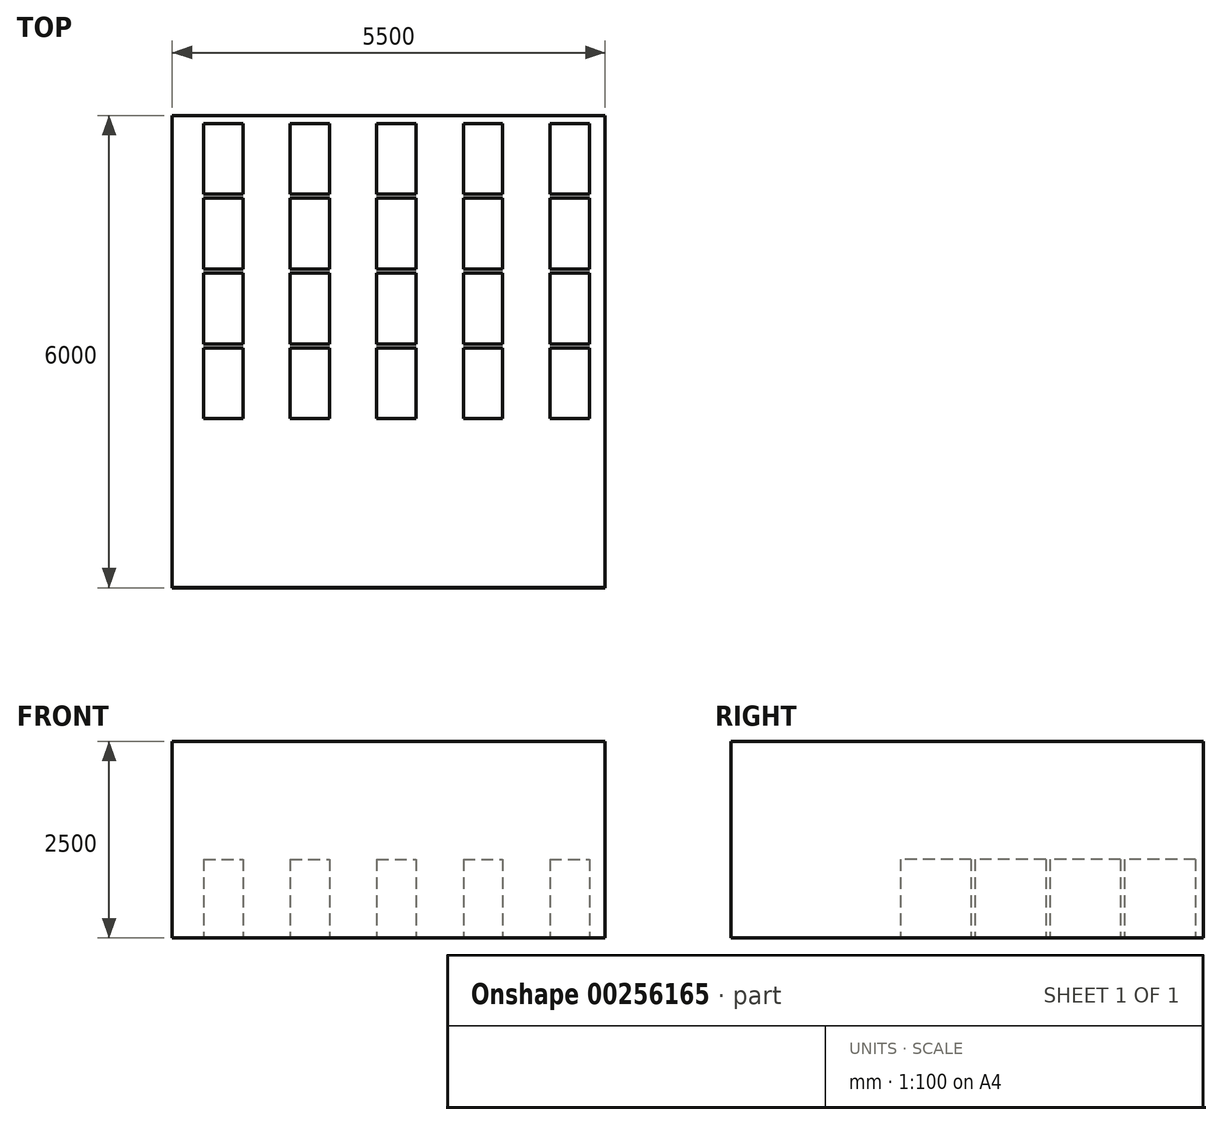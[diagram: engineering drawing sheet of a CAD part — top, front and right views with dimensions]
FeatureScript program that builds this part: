
annotation { "Feature Type Name" : "Feature", "Feature Type Description" : "" }
export const myFeature = defineFeature(function(context is Context, id is Id, definition is map)
    precondition{}
    {
        {
            var Q0;
            Q0=qCreatedBy(makeId("Top.planeOp"),FACE);
            var sketch = newSketch(context, id + "F0", { "sketchPlane" : qUnion([Q0])});
            skLineSegment(sketch, "E0.bottom", {"start": v(0, 0) * mm, "end": v(5500, 0) * mm});
            skLineSegment(sketch, "E0.top", {"start": v(0, 6000) * mm, "end": v(5500, 6000) * mm});
            skLineSegment(sketch, "E0.left", {"start": v(0, 0) * mm, "end": v(0, 6000) * mm});
            skLineSegment(sketch, "E0.right", {"start": v(5500, 0) * mm, "end": v(5500, 6000) * mm});
            skSolve(sketch);
        }
        {
            var Q0;
            Q0 = qSketchRegion(id + "F0", true);
            extrude(context, id + "F1", {"entities" : qUnion([Q0]), "depth" : 2500 * mm});
        }
        {
            var Q0;
            Q0=makeQuery(id+"F1.opExtrude","CAP_FACE",FACE,{"disambiguationData":[OSD([sQuery(id+"F0.wireOp",EDGE,"E0.bottom"),sQuery(id+"F0.wireOp",EDGE,"E0.top"),sQuery(id+"F0.wireOp",EDGE,"E0.left"),sQuery(id+"F0.wireOp",EDGE,"E0.right")])],"isStart":false});
            shell(context, id + "F2", {"entities" : qUnion([Q0]), "thickness" : 1.5 * mm});
        }
        {
            var Q0;
            Q0=makeQuery(id+"F2.opShell","OFFSET_FACE",FACE,{"disambiguationData":[OSD([sQuery(id+"F0.wireOp",EDGE,"E0.bottom"),sQuery(id+"F0.wireOp",EDGE,"E0.top"),sQuery(id+"F0.wireOp",EDGE,"E0.left"),sQuery(id+"F0.wireOp",EDGE,"E0.right")])]});
            var sketch = newSketch(context, id + "F3", { "sketchPlane" : qUnion([Q0])});
            skLineSegment(sketch, "E1.bottom", {"start": v(4798.5, 5898.5) * mm, "end": v(5298.5, 5898.5) * mm});
            skLineSegment(sketch, "E1.top", {"start": v(4798.5, 4998.5) * mm, "end": v(5298.5, 4998.5) * mm});
            skLineSegment(sketch, "E1.left", {"start": v(4798.5, 5898.5) * mm, "end": v(4798.5, 4998.5) * mm});
            skLineSegment(sketch, "E1.right", {"start": v(5298.5, 5898.5) * mm, "end": v(5298.5, 4998.5) * mm});
            skLineSegment(sketch, "E2.0.1.0", {"start": v(4798.5, 4948.5) * mm, "end": v(5298.5, 4948.5) * mm});
            skLineSegment(sketch, "E2.0.1.1", {"start": v(5298.5, 4948.5) * mm, "end": v(5298.5, 4048.5) * mm});
            skLineSegment(sketch, "E2.0.1.2", {"start": v(4798.5, 4048.5) * mm, "end": v(5298.5, 4048.5) * mm});
            skLineSegment(sketch, "E2.0.1.3", {"start": v(4798.5, 4948.5) * mm, "end": v(4798.5, 4048.5) * mm});
            skLineSegment(sketch, "E2.0.2.0", {"start": v(4798.5, 3998.5) * mm, "end": v(5298.5, 3998.5) * mm});
            skLineSegment(sketch, "E2.0.2.1", {"start": v(5298.5, 3998.5) * mm, "end": v(5298.5, 3098.5) * mm});
            skLineSegment(sketch, "E2.0.2.2", {"start": v(4798.5, 3098.5) * mm, "end": v(5298.5, 3098.5) * mm});
            skLineSegment(sketch, "E2.0.2.3", {"start": v(4798.5, 3998.5) * mm, "end": v(4798.5, 3098.5) * mm});
            skLineSegment(sketch, "E2.0.3.0", {"start": v(4798.5, 3048.5) * mm, "end": v(5298.5, 3048.5) * mm});
            skLineSegment(sketch, "E2.0.3.1", {"start": v(5298.5, 3048.5) * mm, "end": v(5298.5, 2148.5) * mm});
            skLineSegment(sketch, "E2.0.3.2", {"start": v(4798.5, 2148.5) * mm, "end": v(5298.5, 2148.5) * mm});
            skLineSegment(sketch, "E2.0.3.3", {"start": v(4798.5, 3048.5) * mm, "end": v(4798.5, 2148.5) * mm});
            skLineSegment(sketch, "E2.1.0.0", {"start": v(3698.5, 5898.5) * mm, "end": v(4198.5, 5898.5) * mm});
            skLineSegment(sketch, "E2.1.0.1", {"start": v(4198.5, 5898.5) * mm, "end": v(4198.5, 4998.5) * mm});
            skLineSegment(sketch, "E2.1.0.2", {"start": v(3698.5, 4998.5) * mm, "end": v(4198.5, 4998.5) * mm});
            skLineSegment(sketch, "E2.1.0.3", {"start": v(3698.5, 5898.5) * mm, "end": v(3698.5, 4998.5) * mm});
            skLineSegment(sketch, "E2.1.1.0", {"start": v(3698.5, 4948.5) * mm, "end": v(4198.5, 4948.5) * mm});
            skLineSegment(sketch, "E2.1.1.1", {"start": v(4198.5, 4948.5) * mm, "end": v(4198.5, 4048.5) * mm});
            skLineSegment(sketch, "E2.1.1.2", {"start": v(3698.5, 4048.5) * mm, "end": v(4198.5, 4048.5) * mm});
            skLineSegment(sketch, "E2.1.1.3", {"start": v(3698.5, 4948.5) * mm, "end": v(3698.5, 4048.5) * mm});
            skLineSegment(sketch, "E2.1.2.0", {"start": v(3698.5, 3998.5) * mm, "end": v(4198.5, 3998.5) * mm});
            skLineSegment(sketch, "E2.1.2.1", {"start": v(4198.5, 3998.5) * mm, "end": v(4198.5, 3098.5) * mm});
            skLineSegment(sketch, "E2.1.2.2", {"start": v(3698.5, 3098.5) * mm, "end": v(4198.5, 3098.5) * mm});
            skLineSegment(sketch, "E2.1.2.3", {"start": v(3698.5, 3998.5) * mm, "end": v(3698.5, 3098.5) * mm});
            skLineSegment(sketch, "E2.1.3.0", {"start": v(3698.5, 3048.5) * mm, "end": v(4198.5, 3048.5) * mm});
            skLineSegment(sketch, "E2.1.3.1", {"start": v(4198.5, 3048.5) * mm, "end": v(4198.5, 2148.5) * mm});
            skLineSegment(sketch, "E2.1.3.2", {"start": v(3698.5, 2148.5) * mm, "end": v(4198.5, 2148.5) * mm});
            skLineSegment(sketch, "E2.1.3.3", {"start": v(3698.5, 3048.5) * mm, "end": v(3698.5, 2148.5) * mm});
            skLineSegment(sketch, "E2.2.0.0", {"start": v(2598.5, 5898.5) * mm, "end": v(3098.5, 5898.5) * mm});
            skLineSegment(sketch, "E2.2.0.1", {"start": v(3098.5, 5898.5) * mm, "end": v(3098.5, 4998.5) * mm});
            skLineSegment(sketch, "E2.2.0.2", {"start": v(2598.5, 4998.5) * mm, "end": v(3098.5, 4998.5) * mm});
            skLineSegment(sketch, "E2.2.0.3", {"start": v(2598.5, 5898.5) * mm, "end": v(2598.5, 4998.5) * mm});
            skLineSegment(sketch, "E2.2.1.0", {"start": v(2598.5, 4948.5) * mm, "end": v(3098.5, 4948.5) * mm});
            skLineSegment(sketch, "E2.2.1.1", {"start": v(3098.5, 4948.5) * mm, "end": v(3098.5, 4048.5) * mm});
            skLineSegment(sketch, "E2.2.1.2", {"start": v(2598.5, 4048.5) * mm, "end": v(3098.5, 4048.5) * mm});
            skLineSegment(sketch, "E2.2.1.3", {"start": v(2598.5, 4948.5) * mm, "end": v(2598.5, 4048.5) * mm});
            skLineSegment(sketch, "E2.2.2.0", {"start": v(2598.5, 3998.5) * mm, "end": v(3098.5, 3998.5) * mm});
            skLineSegment(sketch, "E2.2.2.1", {"start": v(3098.5, 3998.5) * mm, "end": v(3098.5, 3098.5) * mm});
            skLineSegment(sketch, "E2.2.2.2", {"start": v(2598.5, 3098.5) * mm, "end": v(3098.5, 3098.5) * mm});
            skLineSegment(sketch, "E2.2.2.3", {"start": v(2598.5, 3998.5) * mm, "end": v(2598.5, 3098.5) * mm});
            skLineSegment(sketch, "E2.2.3.0", {"start": v(2598.5, 3048.5) * mm, "end": v(3098.5, 3048.5) * mm});
            skLineSegment(sketch, "E2.2.3.1", {"start": v(3098.5, 3048.5) * mm, "end": v(3098.5, 2148.5) * mm});
            skLineSegment(sketch, "E2.2.3.2", {"start": v(2598.5, 2148.5) * mm, "end": v(3098.5, 2148.5) * mm});
            skLineSegment(sketch, "E2.2.3.3", {"start": v(2598.5, 3048.5) * mm, "end": v(2598.5, 2148.5) * mm});
            skLineSegment(sketch, "E2.3.0.0", {"start": v(1498.5, 5898.5) * mm, "end": v(1998.5, 5898.5) * mm});
            skLineSegment(sketch, "E2.3.0.1", {"start": v(1998.5, 5898.5) * mm, "end": v(1998.5, 4998.5) * mm});
            skLineSegment(sketch, "E2.3.0.2", {"start": v(1498.5, 4998.5) * mm, "end": v(1998.5, 4998.5) * mm});
            skLineSegment(sketch, "E2.3.0.3", {"start": v(1498.5, 5898.5) * mm, "end": v(1498.5, 4998.5) * mm});
            skLineSegment(sketch, "E2.3.1.0", {"start": v(1498.5, 4948.5) * mm, "end": v(1998.5, 4948.5) * mm});
            skLineSegment(sketch, "E2.3.1.1", {"start": v(1998.5, 4948.5) * mm, "end": v(1998.5, 4048.5) * mm});
            skLineSegment(sketch, "E2.3.1.2", {"start": v(1498.5, 4048.5) * mm, "end": v(1998.5, 4048.5) * mm});
            skLineSegment(sketch, "E2.3.1.3", {"start": v(1498.5, 4948.5) * mm, "end": v(1498.5, 4048.5) * mm});
            skLineSegment(sketch, "E2.3.2.0", {"start": v(1498.5, 3998.5) * mm, "end": v(1998.5, 3998.5) * mm});
            skLineSegment(sketch, "E2.3.2.1", {"start": v(1998.5, 3998.5) * mm, "end": v(1998.5, 3098.5) * mm});
            skLineSegment(sketch, "E2.3.2.2", {"start": v(1498.5, 3098.5) * mm, "end": v(1998.5, 3098.5) * mm});
            skLineSegment(sketch, "E2.3.2.3", {"start": v(1498.5, 3998.5) * mm, "end": v(1498.5, 3098.5) * mm});
            skLineSegment(sketch, "E2.3.3.0", {"start": v(1498.5, 3048.5) * mm, "end": v(1998.5, 3048.5) * mm});
            skLineSegment(sketch, "E2.3.3.1", {"start": v(1998.5, 3048.5) * mm, "end": v(1998.5, 2148.5) * mm});
            skLineSegment(sketch, "E2.3.3.2", {"start": v(1498.5, 2148.5) * mm, "end": v(1998.5, 2148.5) * mm});
            skLineSegment(sketch, "E2.3.3.3", {"start": v(1498.5, 3048.5) * mm, "end": v(1498.5, 2148.5) * mm});
            skLineSegment(sketch, "E2.4.0.0", {"start": v(398.5, 5898.5) * mm, "end": v(898.5, 5898.5) * mm});
            skLineSegment(sketch, "E2.4.0.1", {"start": v(898.5, 5898.5) * mm, "end": v(898.5, 4998.5) * mm});
            skLineSegment(sketch, "E2.4.0.2", {"start": v(398.5, 4998.5) * mm, "end": v(898.5, 4998.5) * mm});
            skLineSegment(sketch, "E2.4.0.3", {"start": v(398.5, 5898.5) * mm, "end": v(398.5, 4998.5) * mm});
            skLineSegment(sketch, "E2.4.1.0", {"start": v(398.5, 4948.5) * mm, "end": v(898.5, 4948.5) * mm});
            skLineSegment(sketch, "E2.4.1.1", {"start": v(898.5, 4948.5) * mm, "end": v(898.5, 4048.5) * mm});
            skLineSegment(sketch, "E2.4.1.2", {"start": v(398.5, 4048.5) * mm, "end": v(898.5, 4048.5) * mm});
            skLineSegment(sketch, "E2.4.1.3", {"start": v(398.5, 4948.5) * mm, "end": v(398.5, 4048.5) * mm});
            skLineSegment(sketch, "E2.4.2.0", {"start": v(398.5, 3998.5) * mm, "end": v(898.5, 3998.5) * mm});
            skLineSegment(sketch, "E2.4.2.1", {"start": v(898.5, 3998.5) * mm, "end": v(898.5, 3098.5) * mm});
            skLineSegment(sketch, "E2.4.2.2", {"start": v(398.5, 3098.5) * mm, "end": v(898.5, 3098.5) * mm});
            skLineSegment(sketch, "E2.4.2.3", {"start": v(398.5, 3998.5) * mm, "end": v(398.5, 3098.5) * mm});
            skLineSegment(sketch, "E2.4.3.0", {"start": v(398.5, 3048.5) * mm, "end": v(898.5, 3048.5) * mm});
            skLineSegment(sketch, "E2.4.3.1", {"start": v(898.5, 3048.5) * mm, "end": v(898.5, 2148.5) * mm});
            skLineSegment(sketch, "E2.4.3.2", {"start": v(398.5, 2148.5) * mm, "end": v(898.5, 2148.5) * mm});
            skLineSegment(sketch, "E2.4.3.3", {"start": v(398.5, 3048.5) * mm, "end": v(398.5, 2148.5) * mm});
            skLineSegment(sketch, "E2.direction1", {"start": v(4798.5, 4998.5) * mm, "end": v(3698.5, 4998.5) * mm, "construction": true});
            skLineSegment(sketch, "E2.direction2", {"start": v(4798.5, 4998.5) * mm, "end": v(4798.5, 4048.5) * mm, "construction": true});
            skSolve(sketch);
        }
        {
            var Q0;
            Q0 = qSketchRegion(id + "F3", true);
            extrude(context, id + "F4", {"entities" : qUnion([Q0]), "operationType" : NewBodyOperationType.ADD, "depth" : 1000 * mm});
        }
    });
